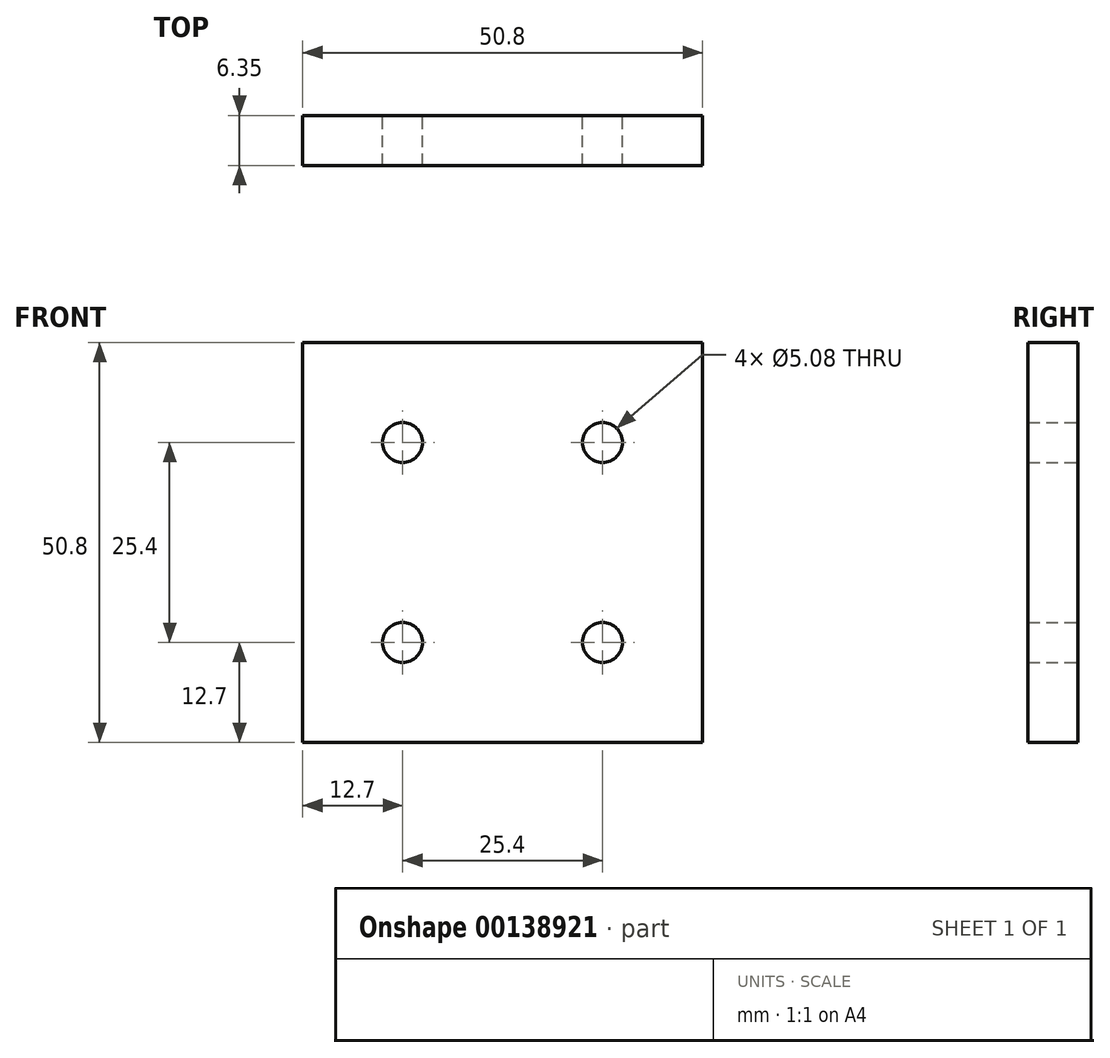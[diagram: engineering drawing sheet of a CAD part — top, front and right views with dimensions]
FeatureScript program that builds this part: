
annotation { "Feature Type Name" : "Feature", "Feature Type Description" : "" }
export const myFeature = defineFeature(function(context is Context, id is Id, definition is map)
    precondition{}
    {
        {
            var Q0;
            Q0=qCreatedBy(makeId("Front.planeOp"),FACE);
            var sketch = newSketch(context, id + "F0", { "sketchPlane" : qUnion([Q0])});
            skLineSegment(sketch, "E0.bottom", {"start": v(25.4, 25.4) * mm, "end": v(-25.4, 25.4) * mm});
            skLineSegment(sketch, "E0.top", {"start": v(25.4, -25.4) * mm, "end": v(-25.4, -25.4) * mm});
            skLineSegment(sketch, "E0.left", {"start": v(25.4, 25.4) * mm, "end": v(25.4, -25.4) * mm});
            skLineSegment(sketch, "E0.right", {"start": v(-25.4, 25.4) * mm, "end": v(-25.4, -25.4) * mm});
            skPoint(sketch, "E0.middle", {"position": v(0, 0) * mm});
            skLineSegment(sketch, "E1", {"start": v(-25.4, 0) * mm, "end": v(25.4, 0) * mm, "construction": true});
            skLineSegment(sketch, "E2", {"start": v(0, 25.4) * mm, "end": v(0, -25.4) * mm, "construction": true});
            skLineSegment(sketch, "E3", {"start": v(-12.7, 25.4) * mm, "end": v(-12.7, -25.4) * mm, "construction": true});
            skLineSegment(sketch, "E4", {"start": v(12.7, 25.4) * mm, "end": v(12.7, -25.4) * mm, "construction": true});
            skLineSegment(sketch, "E5", {"start": v(-25.4, -12.7) * mm, "end": v(25.4, -12.7) * mm, "construction": true});
            skLineSegment(sketch, "E6", {"start": v(-25.4, 12.7) * mm, "end": v(25.4, 12.7) * mm, "construction": true});
            skCircle(sketch, "E7", {"center": v(-12.7, 12.7) * mm, "radius": 2.54 * mm});
            skCircle(sketch, "E8", {"center": v(12.7, 12.7) * mm, "radius": 2.54 * mm});
            skCircle(sketch, "E9", {"center": v(12.7, -12.7) * mm, "radius": 2.54 * mm});
            skCircle(sketch, "E10", {"center": v(-12.7, -12.7) * mm, "radius": 2.54 * mm});
            skSolve(sketch);
        }
        {
            var Q0;
            Q0=makeQuery(id+"F0.imprint","IMPRINT",FACE,{"disambiguationData":[TD([[makeQuery(id+"F0.imprint","IMPRINT",EDGE,{"derivedFrom":sQuery(id+"F0.wireOp",EDGE,"E0.bottom")}),1.0]])]});
            extrude(context, id + "F1", {"entities" : qUnion([Q0]), "depth" : 6.35 * mm});
        }
    });
